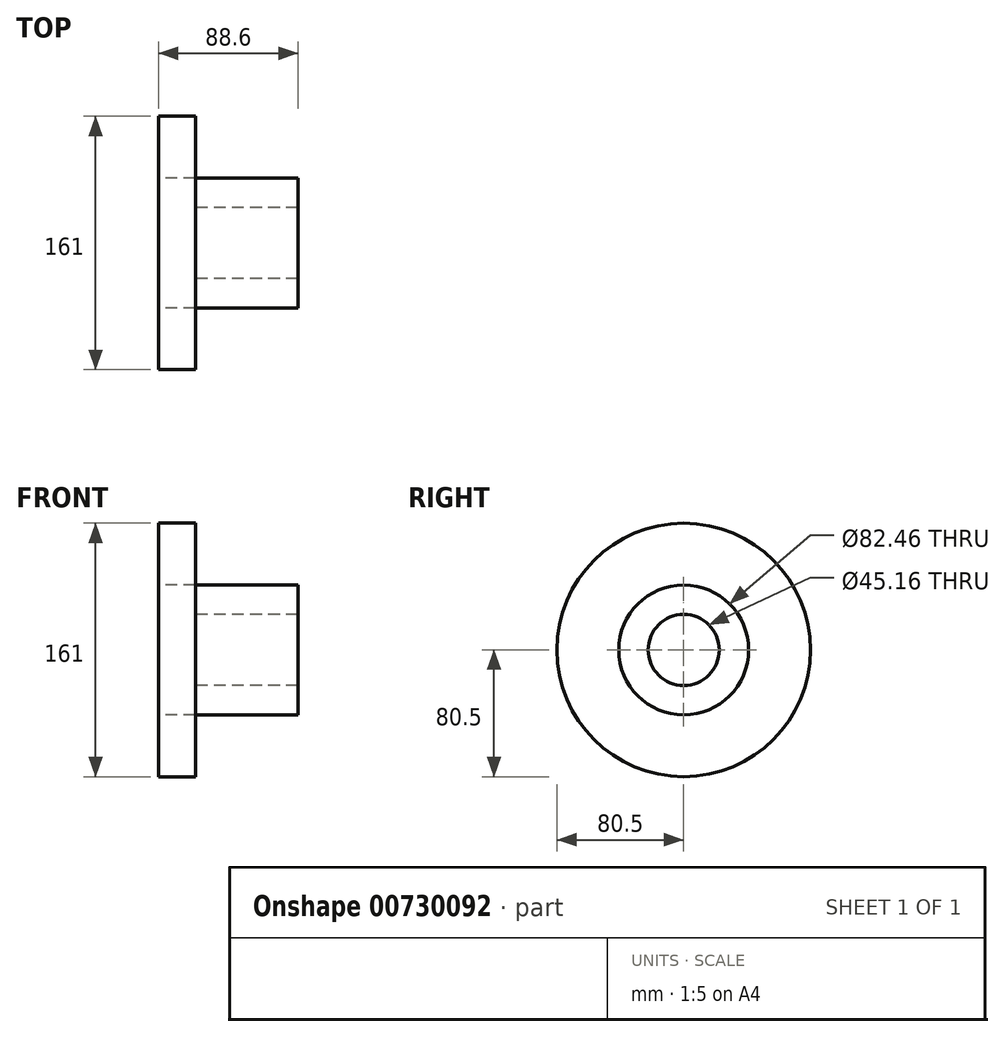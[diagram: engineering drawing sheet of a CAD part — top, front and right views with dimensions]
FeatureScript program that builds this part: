
annotation { "Feature Type Name" : "Feature", "Feature Type Description" : "" }
export const myFeature = defineFeature(function(context is Context, id is Id, definition is map)
    precondition{}
    {
        {
            var Q0;
            Q0=qCreatedBy(makeId("Top.planeOp"),FACE);
            var sketch = newSketch(context, id + "F0", { "sketchPlane" : qUnion([Q0])});
            skLineSegment(sketch, "E0.bottom", {"start": v(0, 22.58) * mm, "end": v(23.32, 22.58) * mm});
            skLineSegment(sketch, "E0.top", {"start": v(0, 80.5) * mm, "end": v(23.32, 80.5) * mm});
            skLineSegment(sketch, "E0.left", {"start": v(0, 22.58) * mm, "end": v(0, 80.5) * mm});
            skLineSegment(sketch, "E0.right", {"start": v(23.32, 22.58) * mm, "end": v(23.32, 80.5) * mm});
            skPoint(sketch, "E1.oppositeSnap0", {"position": v(11.66, 22.58) * mm});
            skLineSegment(sketch, "E1.bottom", {"start": v(0, 41.23) * mm, "end": v(88.6, 41.23) * mm});
            skLineSegment(sketch, "E1.top", {"start": v(0, 22.58) * mm, "end": v(88.6, 22.58) * mm});
            skLineSegment(sketch, "E1.left", {"start": v(0, 41.23) * mm, "end": v(0, 22.58) * mm});
            skLineSegment(sketch, "E1.right", {"start": v(88.6, 41.23) * mm, "end": v(88.6, 22.58) * mm});
            skLineSegment(sketch, "E2.bottom", {"start": v(0, 0) * mm, "end": v(88.6, 0) * mm, "construction": true});
            skLineSegment(sketch, "E2.top", {"start": v(0, 0) * mm, "end": v(88.6, 0) * mm, "construction": true});
            skLineSegment(sketch, "E2.left", {"start": v(0, 0) * mm, "end": v(0, 0) * mm});
            skLineSegment(sketch, "E2.right", {"start": v(88.6, 0) * mm, "end": v(88.6, 0) * mm});
            skLineSegment(sketch, "E3.MirrorCS", {"start": v(0, -22.58) * mm, "end": v(23.32, -22.58) * mm});
            skLineSegment(sketch, "E4.MirrorCS", {"start": v(0, -80.5) * mm, "end": v(23.32, -80.5) * mm});
            skPoint(sketch, "E5.MirrorP", {"position": v(11.66, -22.58) * mm});
            skLineSegment(sketch, "E6.MirrorCS", {"start": v(0, -22.58) * mm, "end": v(0, -80.5) * mm});
            skLineSegment(sketch, "E7.MirrorCS", {"start": v(23.32, -22.58) * mm, "end": v(23.32, -80.5) * mm});
            skLineSegment(sketch, "E8.MirrorCS", {"start": v(0, -41.23) * mm, "end": v(88.6, -41.23) * mm});
            skLineSegment(sketch, "E9.MirrorCS", {"start": v(0, -22.58) * mm, "end": v(88.6, -22.58) * mm});
            skLineSegment(sketch, "E10.MirrorCS", {"start": v(0, -41.23) * mm, "end": v(0, -22.58) * mm});
            skLineSegment(sketch, "E11.MirrorCS", {"start": v(88.6, -41.23) * mm, "end": v(88.6, -22.58) * mm});
            skSolve(sketch);
        }
        {
            var Q0;
            {var subQ0=sQuery(id+"F0.wireOp",EDGE,"E0.top");Q0=makeQuery(id+"F0.imprint","IMPRINT",FACE,{"disambiguationData":[TD([[makeQuery(id+"F0.imprint","IMPRINT",EDGE,{"derivedFrom":subQ0}),-1.0]])]});}
            var Q1;
            {var subQ5=sQuery(id+"F0.wireOp",EDGE,"E1.left");Q1=makeQuery(id+"F0.imprint","IMPRINT",FACE,{"disambiguationData":[TD([[makeQuery(id+"F0.imprint","IMPRINT",EDGE,{"derivedFrom":subQ5}),1.0]])]});}
            var Q2;
            {var subQ5=sQuery(id+"F0.wireOp",EDGE,"E1.right");Q2=makeQuery(id+"F0.imprint","IMPRINT",FACE,{"disambiguationData":[TD([[makeQuery(id+"F0.imprint","IMPRINT",EDGE,{"derivedFrom":subQ5}),-1.0]])]});}
            var Q3;
            Q3=sQuery(id+"F0.wireOp",EDGE,"E2.top");
            revolve(context, id + "F1", {"surfaceOperationType" : NewSurfaceOperationType.NEW, "entities" : qUnion([Q0, Q1, Q2]), "axis" : qUnion([Q3]), "revolveType" : RevolveType.FULL});
        }
    });
